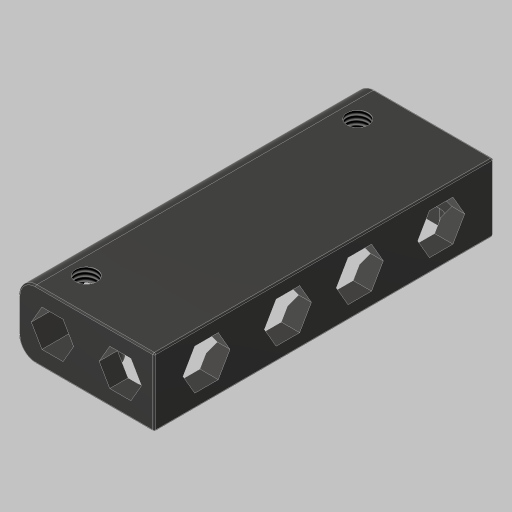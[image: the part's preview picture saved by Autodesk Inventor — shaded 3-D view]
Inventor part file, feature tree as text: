
AUTODESK INVENTOR PART (.ipt)
format: ipt  version: 2023.5 (Build 275446000, 446)  size: 349,184 bytes
history: native  units: in
note: dims shown in document units (in); Inventor stores cm internally (conversion verified against a paired STEP export)
features: sketch x5, extrude x4, fillet x3, projected_geometry x2, hole x1
ambient origin geometry x8: Origin, YZ Plane, XZ Plane, XY Plane, X Axis, Y Axis, Z Axis, Center Point
bodies: Solid1 (feature_tree)
feature tree (15):
  extrude  "Extrusion1"  Depth=0.5in
  hole  "Hole1"  [1 undecoded]
  fillet  "Fillet1"  Radius=0.25in
  fillet  "Fillet2"  Radius=0.125in
  extrude  "Extrusion2"  Depth=0.125in
  fillet  "Fillet3"  Radius=0.125in
  extrude  "Extrusion3"  Depth=0.375in TaperAngle=0.0deg
  extrude  "Extrusion4"  Depth=0.13in
  sketch  "Sketch1"  dims[d0=1.0in d1=0.5in]
  sketch  "Sketch2"  dims[d2=2.5in d3=0.0in d4=2.0in d5=0.25in]
  sketch  "Sketch3"  dims[d6=0.156in d7=0.38in d8=0.385in d9=0.25in d10=0.5635in d11=1.0in d12=0.8108in d13=0.125in]
  sketch  "Sketch4"  dims[d14=0.01in d15=0.125in d16=0.125in]
  sketch  "Sketch5"  dims[d17=0.125in d18=0.375in d19=0.0in d20=0.13in d21=0.3in d22=0.375in d23=0.7874in d25=0.6in d26=0.3937in d28=1.0in d30=0.0in d31=0.0in d32=0.25in d33=0.0in d34=0.0in]
  projected_geometry  "Project Cut Edges1"
  projected_geometry  "Project Cut Edges2"
note: 1 required parameter value undecoded (feature->parameter linkage not recoverable at this tier; creation-order binding heuristic only, values carry confidence <= 0.55)
